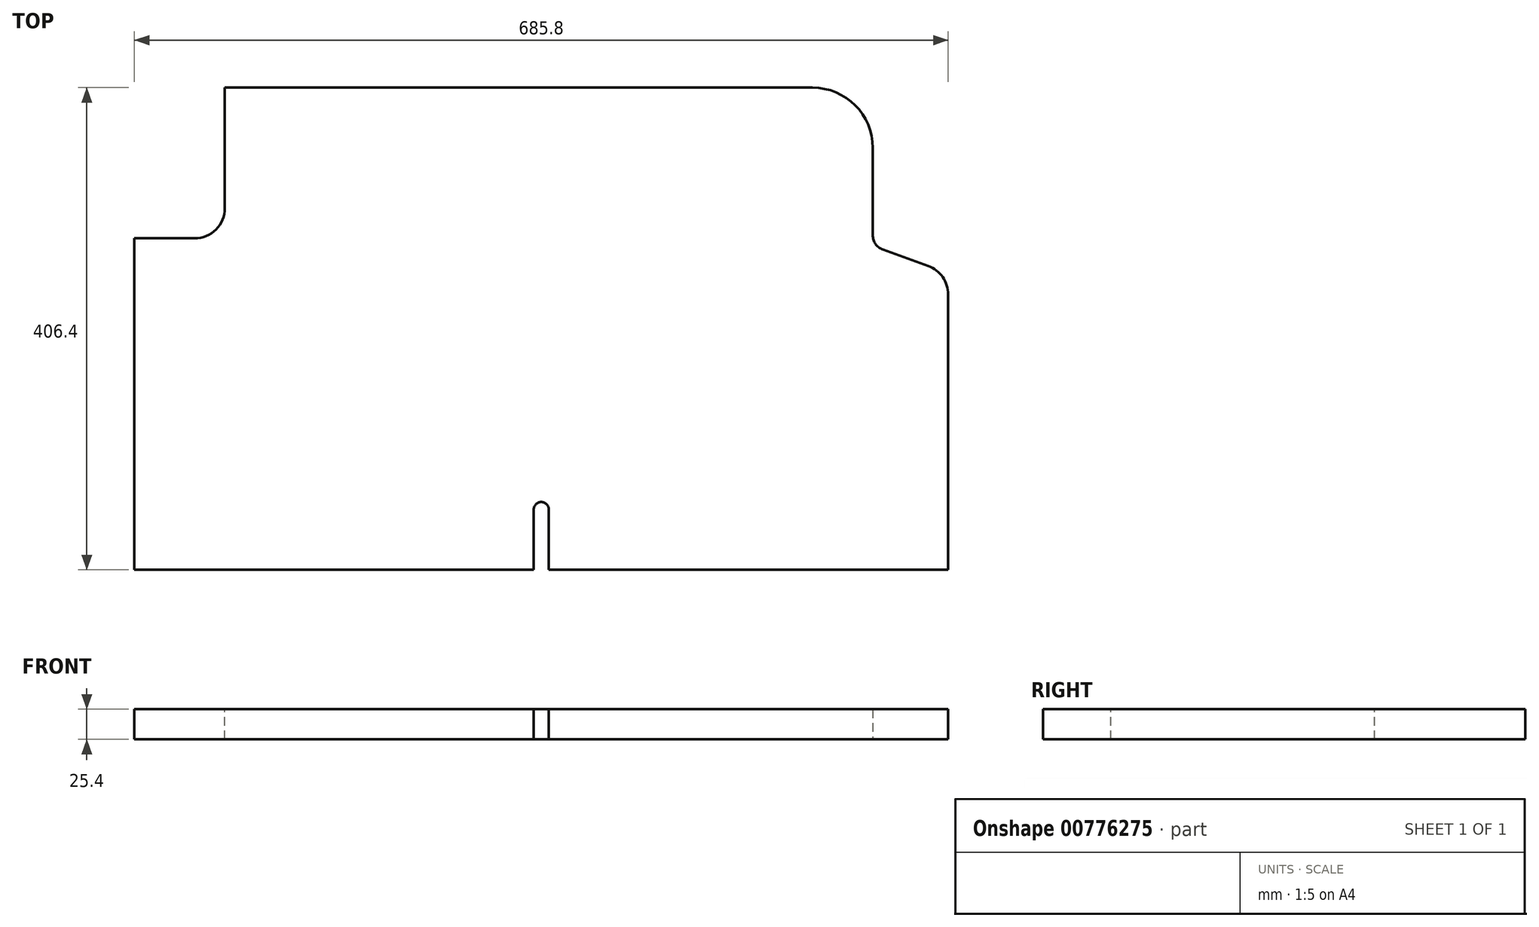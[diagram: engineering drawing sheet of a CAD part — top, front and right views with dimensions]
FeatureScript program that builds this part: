
annotation { "Feature Type Name" : "Feature", "Feature Type Description" : "" }
export const myFeature = defineFeature(function(context is Context, id is Id, definition is map)
    precondition{}
    {
        {
            var Q0;
            Q0=qCreatedBy(makeId("Top.planeOp"),FACE);
            var sketch = newSketch(context, id + "F0", { "sketchPlane" : qUnion([Q0])});
            skLineSegment(sketch, "E0.bottom", {"start": v(-286.27, 201.9) * mm, "end": v(412.23, 201.9) * mm});
            skLineSegment(sketch, "E0.top", {"start": v(-286.27, -204.5) * mm, "end": v(412.23, -204.5) * mm});
            skLineSegment(sketch, "E0.left", {"start": v(-286.27, 201.9) * mm, "end": v(-286.27, -204.5) * mm});
            skLineSegment(sketch, "E0.right", {"start": v(412.23, 201.9) * mm, "end": v(412.23, -204.5) * mm});
            skSolve(sketch);
        }
        {
            var Q0;
            Q0 = qSketchRegion(id + "F0", true);
            extrude(context, id + "F1", {"entities" : qUnion([Q0]), "depth" : 25.4 * mm, "offsetDistance" : 25.4 * mm});
        }
        {
            var Q0;
            Q0=makeQuery(id+"F1.opExtrude","CAP_FACE",FACE,{"disambiguationData":[OSD([sQuery(id+"F0.wireOp",EDGE,"E0.bottom"),sQuery(id+"F0.wireOp",EDGE,"E0.top"),sQuery(id+"F0.wireOp",EDGE,"E0.left"),sQuery(id+"F0.wireOp",EDGE,"E0.right")])],"isStart":false});
            var sketch = newSketch(context, id + "F2", { "sketchPlane" : qUnion([Q0])});
            skArc(sketch, "E1", {"start": v(336.03, 77.43) * mm, "mid": v(338.33, 70.15) * mm, "end": v(344.39, 65.5) * mm});
            skLineSegment(sketch, "E2", {"start": v(336.03, 77.43) * mm, "end": v(336.03, 284.54) * mm});
            skLineSegment(sketch, "E3", {"start": v(344.39, 65.5) * mm, "end": v(488.18, 13.16) * mm});
            skLineSegment(sketch, "E4", {"start": v(336.03, 284.54) * mm, "end": v(504.16, 284.54) * mm});
            skLineSegment(sketch, "E5", {"start": v(504.16, 284.54) * mm, "end": v(488.18, 13.16) * mm});
            skSolve(sketch);
        }
        {
            var Q0;
            Q0 = qSketchRegion(id + "F2", true);
            extrude(context, id + "F3", {"entities" : qUnion([Q0]), "operationType" : NewBodyOperationType.REMOVE, "oppositeDirection" : true, "depth" : 25.4 * mm, "offsetDistance" : 25.4 * mm});
        }
        {
            var Q0;
            Q0=makeQuery(id+"F1.opExtrude","CAP_FACE",FACE,{"disambiguationData":[OSD([sQuery(id+"F0.wireOp",EDGE,"E0.bottom"),sQuery(id+"F0.wireOp",EDGE,"E0.top"),sQuery(id+"F0.wireOp",EDGE,"E0.left"),sQuery(id+"F0.wireOp",EDGE,"E0.right")])],"isStart":false});
            var sketch = newSketch(context, id + "F4", { "sketchPlane" : qUnion([Q0])});
            skLineSegment(sketch, "E6.bottom", {"start": v(412.23, -204.5) * mm, "end": v(399.53, -204.5) * mm});
            skLineSegment(sketch, "E6.top", {"start": v(412.23, 49.5) * mm, "end": v(399.53, 49.5) * mm});
            skLineSegment(sketch, "E6.left", {"start": v(412.23, -204.5) * mm, "end": v(412.23, 49.5) * mm});
            skLineSegment(sketch, "E6.right", {"start": v(399.53, -204.5) * mm, "end": v(399.53, 49.5) * mm});
            skSolve(sketch);
        }
        {
            var Q0;
            Q0 = qSketchRegion(id + "F4", true);
            extrude(context, id + "F5", {"entities" : qUnion([Q0]), "operationType" : NewBodyOperationType.REMOVE, "oppositeDirection" : true, "depth" : 25.4 * mm, "offsetDistance" : 25.4 * mm});
        }
        {
            var Q0;
            Q0=makeQuery(id+"F3.boolean.opBoolean","INTERSECT",EDGE,{"derivedFrom":[makeQuery(id+"F1.opExtrude","SWEPT_FACE",FACE,{"disambiguationData":[OSD([sQuery(id+"F0.wireOp",EDGE,"E0.bottom")])]}),makeQuery(id+"F3.opExtrude","SWEPT_FACE",FACE,{"disambiguationData":[OSD([sQuery(id+"F2.wireOp",EDGE,"E2")])]})]});
            fillet(context, id + "F6", {"entities" : qUnion([Q0]), "radius" : 50.8 * mm, "tangentPropagation" : true, "allowEdgeOverflow" : false});
        }
        {
            var Q0;
            Q0=makeQuery(id+"F1.opExtrude","CAP_FACE",FACE,{"disambiguationData":[OSD([sQuery(id+"F0.wireOp",EDGE,"E0.bottom"),sQuery(id+"F0.wireOp",EDGE,"E0.top"),sQuery(id+"F0.wireOp",EDGE,"E0.left"),sQuery(id+"F0.wireOp",EDGE,"E0.right")])],"isStart":false});
            var sketch = newSketch(context, id + "F7", { "sketchPlane" : qUnion([Q0])});
            skLineSegment(sketch, "E7.bottom", {"start": v(-286.27, 201.9) * mm, "end": v(-210.07, 201.9) * mm});
            skLineSegment(sketch, "E7.top", {"start": v(-286.27, 74.9) * mm, "end": v(-210.07, 74.9) * mm});
            skLineSegment(sketch, "E7.left", {"start": v(-286.27, 201.9) * mm, "end": v(-286.27, 74.9) * mm});
            skLineSegment(sketch, "E7.right", {"start": v(-210.07, 201.9) * mm, "end": v(-210.07, 74.9) * mm});
            skSolve(sketch);
        }
        {
            var Q0;
            Q0 = qSketchRegion(id + "F7", true);
            extrude(context, id + "F8", {"entities" : qUnion([Q0]), "operationType" : NewBodyOperationType.REMOVE, "oppositeDirection" : true, "depth" : 25.4 * mm, "offsetDistance" : 25.4 * mm});
        }
        {
            var Q0;
            Q0=makeQuery(id+"F8.boolean.opBoolean","COPY",EDGE,{"derivedFrom":makeQuery(id+"F8.opExtrude","SWEPT_EDGE",EDGE,{"disambiguationData":[OSD([sQuery(id+"F7.wireOp",EDGE,"E7.top"),sQuery(id+"F7.wireOp",EDGE,"E7.right")])]})});
            fillet(context, id + "F9", {"entities" : qUnion([Q0]), "radius" : 25.4 * mm, "tangentPropagation" : true, "defaultsChanged" : true, "vertexSettings" : [], "allowEdgeOverflow" : false});
        }
        {
            var Q0;
            Q0=makeQuery(id+"F8.boolean.opBoolean","COPY",EDGE,{"derivedFrom":makeQuery(id+"F8.opExtrude","SWEPT_EDGE",EDGE,{"disambiguationData":[OSD([sQuery(id+"F0.wireOp",EDGE,"E0.bottom"),sQuery(id+"F7.wireOp",EDGE,"E7.bottom"),sQuery(id+"F7.wireOp",EDGE,"E7.right")])]})});
            var Q1;
            Q1=makeQuery(id+"F8.boolean.opBoolean","COPY",EDGE,{"derivedFrom":makeQuery(id+"F8.opExtrude","SWEPT_EDGE",EDGE,{"disambiguationData":[OSD([sQuery(id+"F0.wireOp",EDGE,"E0.left"),sQuery(id+"F7.wireOp",EDGE,"E7.top"),sQuery(id+"F7.wireOp",EDGE,"E7.left")])]})});
            var Q2;
            Q2=makeQuery(id+"F5.boolean.opBoolean","INTERSECT",EDGE,{"derivedFrom":[makeQuery(id+"F3.boolean.opBoolean","COPY",FACE,{"derivedFrom":makeQuery(id+"F3.opExtrude","SWEPT_FACE",FACE,{"disambiguationData":[OSD([sQuery(id+"F2.wireOp",EDGE,"E3")])]})}),makeQuery(id+"F5.opExtrude","SWEPT_FACE",FACE,{"disambiguationData":[OSD([sQuery(id+"F4.wireOp",EDGE,"E6.right")])]})]});
            fillet(context, id + "F10", {"entities" : qUnion([Q0, Q1, Q2]), "radius" : 25.4 * mm, "tangentPropagation" : true, "allowEdgeOverflow" : false});
        }
        {
            var Q0;
            Q0=makeQuery(id+"F1.opExtrude","CAP_FACE",FACE,{"disambiguationData":[OSD([sQuery(id+"F0.wireOp",EDGE,"E0.bottom"),sQuery(id+"F0.wireOp",EDGE,"E0.top"),sQuery(id+"F0.wireOp",EDGE,"E0.left"),sQuery(id+"F0.wireOp",EDGE,"E0.right")])],"isStart":false});
            var sketch = newSketch(context, id + "F11", { "sketchPlane" : qUnion([Q0])});
            skArc(sketch, "E8", {"start": v(62.98, -153.7) * mm, "mid": v(56.63, -147.36) * mm, "end": v(50.28, -153.7) * mm});
            skLineSegment(sketch, "E9", {"start": v(50.28, -153.7) * mm, "end": v(50.28, -204.77) * mm});
            skPoint(sketch, "E9.endSnap0", {"position": v(50.28, -191.8) * mm});
            skLineSegment(sketch, "E10", {"start": v(62.98, -153.7) * mm, "end": v(62.98, -212.46) * mm});
            skLineSegment(sketch, "E11", {"start": v(50.28, -204.77) * mm, "end": v(62.98, -212.46) * mm});
            skSolve(sketch);
        }
        {
            var Q0;
            Q0 = qSketchRegion(id + "F11", true);
            extrude(context, id + "F12", {"entities" : qUnion([Q0]), "operationType" : NewBodyOperationType.REMOVE, "flatOperationType" : FlatOperationType.REMOVE, "endBound" : BoundingType.THROUGH_ALL, "oppositeDirection" : true, "depth" : 25.4 * mm, "offsetDistance" : 25.4 * mm, "domain" : OperationDomain.MODEL});
        }
    });
